# Revit family: 1PRD_FrankeWS_DrnkngFntnPckgs_AnimaDrinkingFountain_DF240WM
name_source: partatom
category: Plumbing Fixtures
revit_build: Autodesk Revit 2015 (Build: 20160512_1515(x64)
units: mm (PartAtom-declared; Revit-internal decimal feet)

## types (1)
- DF240WM
    AssetType = Fixed
    BIMObjectName = PRD_FrankeWS_DrinkingFountainPackages_AnimaDrinkingFountain_DF240WM
    Category = Pr_40_20_87_24, Drinking fountains
    Color = Stainless steel
    Default Elevation = 850 mm  [stored 2.78871 ft]
    Description = Drinking fountain for wall mounting, stainless steel, surface satin finished, material thickness 1 mm, seamless welded round bowl with diameter 240 mm, semicircular shape, 45 mm tap ledge, without overflow, 1 1/2 inch. flat perforated waste, drainage centric, incl. premounted 3/8 inch. manual self closing drinking bubbler, incl. screws and dowels.
    DrainSize = DN-40-1-1-2INH
    DrinkingFountainMaterial = PRD_FrankeWS_StainlessSteel_SatinFinished
    DurationUnit = year
    Features = stainless steel, 1.00 mm, satin finished, wall mounting, 315x105x320 mm (WxHxD)
    Finish = Satin finished
    Flow = 0.1 L/s
    FormUnit = Wall mounted
    FormWastes = DN-40-1-1-2INH
    FountainType = DrinkingWater
    GrossWeight = 3.00 kg
    IfcExportAs = IfcSanitaryTerminalType
    IfcExportType = SANITARYFOUNTAIN
    Inlet = 1/2"
    InletSize = G-3-8-B
    IntegralAccessories = Incl. premounted manual self closing drinking bubbler, incl. screws and dowels.
    Manufacturer = FRANKE Water Systems AG
    ManufacturerName = FRANKE Water Systems AG
    ManufacturerURL = www.franke.com
    Material = Stainless steel
    MaterialsBody = Stainless steel 1.4301
    Model = DF240WM
    ModelNumber = 2000057389
    ModelReference = DF240WM
    Mounting = WallHung
    NBSDescription = Drinking fountain packages
    NBSReference = 45-35-70/400
    Name = ANIMA drinking fountain DF240WM
    NetWeight = 2.56 kg
    NominalDepth = 320 mm  [stored 1.04987 ft]
    NominalHeight = 105 mm  [stored 0.344488 ft]
    NominalLength = 0 mm  [stored 0 ft]
    NominalWidth = 315 mm  [stored 1.03346 ft]
    ProductInformation = http://igh.franke.mycontent.ch
    Size = 315 x 105 x 320 mm
    TapMaterial = PRD_FrankeWS_ChromatedBrass_HighPolished
    URL = www.franke.com
    Uniclass2015Code = Pr_40_20_87_24
    Uniclass2015Title = Drinking fountains
    Uniclass2015Version = Products v1.5
    Version = 1
    WarrantyDurationUnit = year
    WasteSize = 1 1/2"

note: [stored X ft] marks values corroborated as IEEE doubles in the binary element streams (Revit-internal decimal feet)

## geometry (parser evidence)
native form markers: Sweep x6
no freeform markers — native parametric forms only
